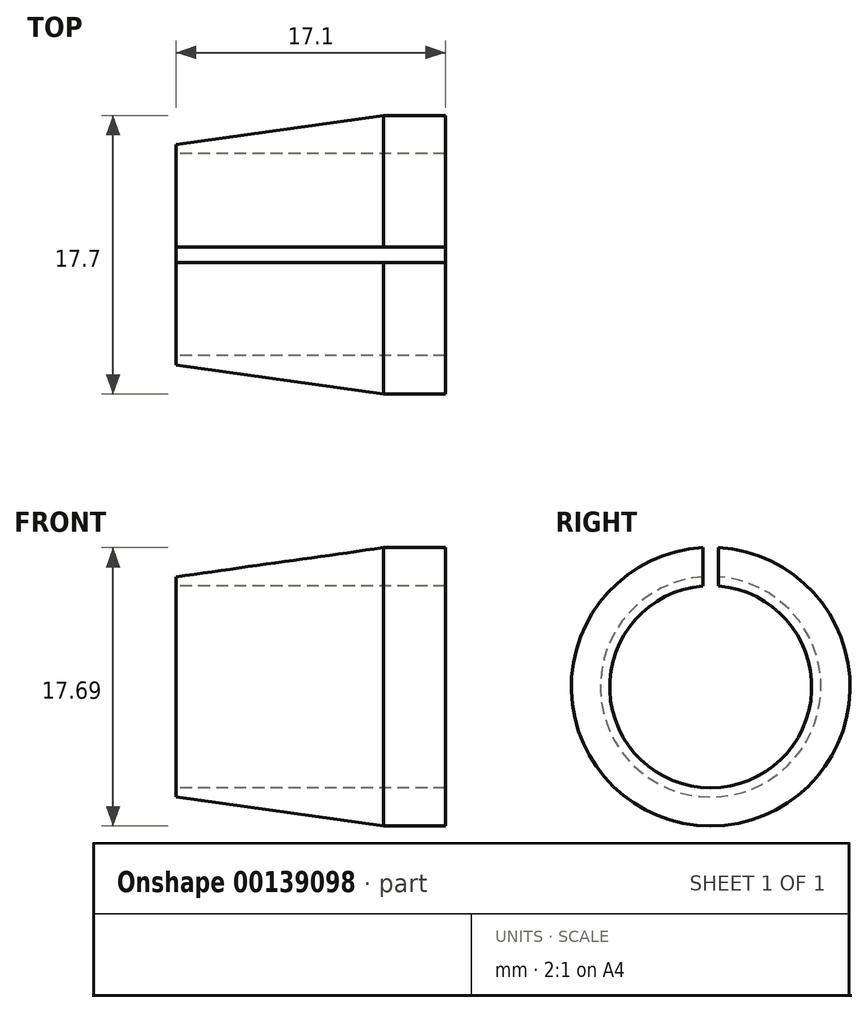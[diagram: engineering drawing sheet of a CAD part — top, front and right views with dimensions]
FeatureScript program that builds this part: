
annotation { "Feature Type Name" : "Feature", "Feature Type Description" : "" }
export const myFeature = defineFeature(function(context is Context, id is Id, definition is map)
    precondition{}
    {
        {
            var Q0;
            Q0=qCreatedBy(makeId("Front.planeOp"),FACE);
            var sketch = newSketch(context, id + "F0", { "sketchPlane" : qUnion([Q0])});
            skLineSegment(sketch, "E0", {"start": v(0, 0) * mm, "end": v(27.14, 0) * mm, "construction": true});
            skLineSegment(sketch, "E1", {"start": v(0, 0) * mm, "end": v(0, 21.05) * mm, "construction": true});
            skLineSegment(sketch, "E2", {"start": v(0, 6.41) * mm, "end": v(17.1, 6.41) * mm});
            skLineSegment(sketch, "E3", {"start": v(17.1, 6.41) * mm, "end": v(17.1, 8.85) * mm});
            skLineSegment(sketch, "E4", {"start": v(17.1, 8.85) * mm, "end": v(13.16, 8.85) * mm});
            skLineSegment(sketch, "E5", {"start": v(13.16, 8.85) * mm, "end": v(0, 7) * mm});
            skLineSegment(sketch, "E6", {"start": v(0, 7) * mm, "end": v(0, 6.41) * mm});
            skSolve(sketch);
        }
        {
            var Q0;
            Q0 = qSketchRegion(id + "F0", true);
            var Q1;
            Q1=sQuery(id+"F0.wireOp",EDGE,"E0");
            revolve(context, id + "F1", {"entities" : qUnion([Q0]), "axis" : qUnion([Q1]), "revolveType" : RevolveType.FULL});
        }
        {
            var Q0;
            Q0=makeQuery(id+"F1.opRevolve","SWEPT_FACE",FACE,{"disambiguationData":[OSD([sQuery(id+"F0.wireOp",EDGE,"E3")])]});
            var sketch = newSketch(context, id + "F2", { "sketchPlane" : qUnion([Q0])});
            skLineSegment(sketch, "E7.bottom", {"start": v(-0.5, 0) * mm, "end": v(0.5, 0) * mm});
            skLineSegment(sketch, "E7.top", {"start": v(-0.5, 11.17) * mm, "end": v(0.5, 11.17) * mm});
            skLineSegment(sketch, "E7.left", {"start": v(-0.5, 0) * mm, "end": v(-0.5, 11.17) * mm});
            skLineSegment(sketch, "E7.right", {"start": v(0.5, 0) * mm, "end": v(0.5, 11.17) * mm});
            skLineSegment(sketch, "E8", {"start": v(0, 0) * mm, "end": v(0, 6.1) * mm, "construction": true});
            skPoint(sketch, "E8.endSnap0", {"position": v(0, 11.17) * mm});
            skSolve(sketch);
        }
        {
            var Q0;
            Q0 = qSketchRegion(id + "F2", true);
            extrude(context, id + "F3", {"entities" : qUnion([Q0]), "operationType" : NewBodyOperationType.REMOVE, "endBound" : BoundingType.THROUGH_ALL, "oppositeDirection" : true, "depth" : 25 * mm});
        }
    });
